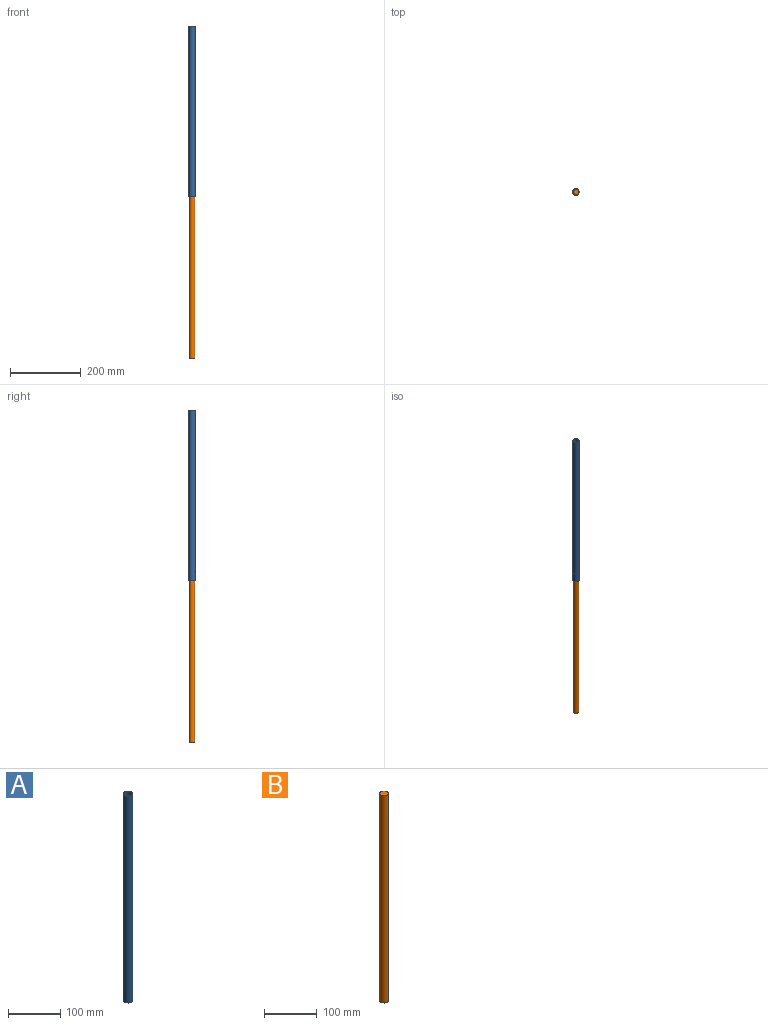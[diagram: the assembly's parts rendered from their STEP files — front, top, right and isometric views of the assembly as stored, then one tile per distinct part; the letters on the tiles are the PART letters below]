
ASSEMBLY  parts=2 mates=1
PART A: 4 faces, bbox 18x18x482.6 mm
  f0: cylinder r=8.06mm len=482.6mm, axis (0,0,-1), area 24453.7mm2, adj f2,f3
  f1: cylinder r=9.02mm len=482.6mm, axis (0,0,-1), area 27341.9mm2, adj f2,f3
  f2: plane 18.03x18.03mm, normal (0,0,1), area 51.1mm2, adj f0,f1
  f3: plane 18.03x18.03mm, normal (0,0,-1), area 51.1mm2, adj f0,f1
PART B: 3 faces, bbox 16.1x16.1x482.6 mm
  f0: cylinder r=8.06mm len=482.6mm, axis (0,0,-1), area 24453.7mm2, adj f1,f2
  f1: plane 16.13x16.13mm, normal (0,0,1), area 204.3mm2, adj f0
  f2: plane 16.13x16.13mm, normal (0,0,-1), area 204.3mm2, adj f0
PLACE A t=(-108.35,264.64,-166.78)mm
PLACE B t=(-108.35,264.64,-166.78)mm
MATE slider B.f0 <-> A.f0  axis (0,0,1) through (-108.35,264.64,315.82)mm
